annotation { "Feature Type Name" : "Feature", "Feature Type Description" : "" }
export const myFeature = defineFeature(function(context is Context, id is Id, definition is map)
    precondition{}
    {
        {
            var Q0;
            Q0=qCreatedBy(makeId("Front.planeOp"),FACE);
            var sketch = newSketch(context, id + "F0", { "sketchPlane" : qUnion([Q0])});
            skLineSegment(sketch, "E0", {"start": v(-56.16, 20.1) * mm, "end": v(36.97, 20.1) * mm});
            skLineSegment(sketch, "E1", {"start": v(36.97, 20.1) * mm, "end": v(36.97, 27.48) * mm});
            skLineSegment(sketch, "E2", {"start": v(36.97, 27.48) * mm, "end": v(-55.57, 27.48) * mm});
            skLineSegment(sketch, "E3", {"start": v(-56.16, 20.1) * mm, "end": v(-56.16, 27.48) * mm});
            skLineSegment(sketch, "E4", {"start": v(-56.16, 27.48) * mm, "end": v(-41.78, 27.48) * mm});
            skLineSegment(sketch, "E5", {"start": v(-41.78, 27.48) * mm, "end": v(36.97, 27.48) * mm});
            skLineSegment(sketch, "E6", {"start": v(-56.16, 29.66) * mm, "end": v(-56.16, 20.1) * mm});
            skSolve(sketch);
        }
        {
            var Q0;
            Q0 = qSketchRegion(id + "F0", true);
            extrude(context, id + "F1", {"entities" : qUnion([Q0]), "depth" : 25.4 * mm});
        }
        {
            var Q0;
            Q0=qCreatedBy(makeId("Front.planeOp"),FACE);
            var sketch = newSketch(context, id + "F2", { "sketchPlane" : qUnion([Q0])});
            skArc(sketch, "E7", {"start": v(37.35, 26.8) * mm, "mid": v(-9.42, 59) * mm, "end": v(-56.08, 26.63) * mm});
            skLineSegment(sketch, "E8", {"start": v(-56.08, 26.63) * mm, "end": v(-58.22, 20.94) * mm});
            skLineSegment(sketch, "E9", {"start": v(-58.22, 20.94) * mm, "end": v(-53.67, 19.22) * mm});
            skLineSegment(sketch, "E10", {"start": v(37.35, 26.8) * mm, "end": v(40.23, 19.22) * mm});
            skLineSegment(sketch, "E11", {"start": v(40.23, 19.22) * mm, "end": v(37.35, 18.13) * mm});
            skSolve(sketch);
        }
        {
            var Q0;
            Q0=sQuery(id+"F2.wireOp",EDGE,"E7");
            extrude(context, id + "F3", {"bodyType" : ToolBodyType.SURFACE, "surfaceEntities" : qUnion([Q0]), "depth" : 25.4 * mm});
        }
        {
            var Q0;
            Q0=qCreatedBy(makeId("Front.planeOp"),FACE);
            var sketch = newSketch(context, id + "F4", { "sketchPlane" : qUnion([Q0])});
            skText(sketch, "E12", { "text": "Dem Dudes", "fontName": "OpenSans-Regular.ttf"});
            skLineSegment(sketch, "E13", {"start": v(-55.97, 19.9) * mm, "end": v(-55.97, 0) * mm});
            skLineSegment(sketch, "E14", {"start": v(-55.97, 0) * mm, "end": v(37.44, 0) * mm});
            skLineSegment(sketch, "E15", {"start": v(37.44, 0) * mm, "end": v(37.44, 20.3) * mm});
            const initialGuessF4  = {"E12": [-0.05006, 0.0274, 1, 0, 0.01064]};
            skSetInitialGuess(sketch, initialGuessF4);
            skSolve(sketch);
        }
        {
            var Q0;
            Q0 = qSketchRegion(id + "F4", true);
            extrude(context, id + "F5", {"entities" : qUnion([Q0]), "depth" : 25.4 * mm});
        }
    });